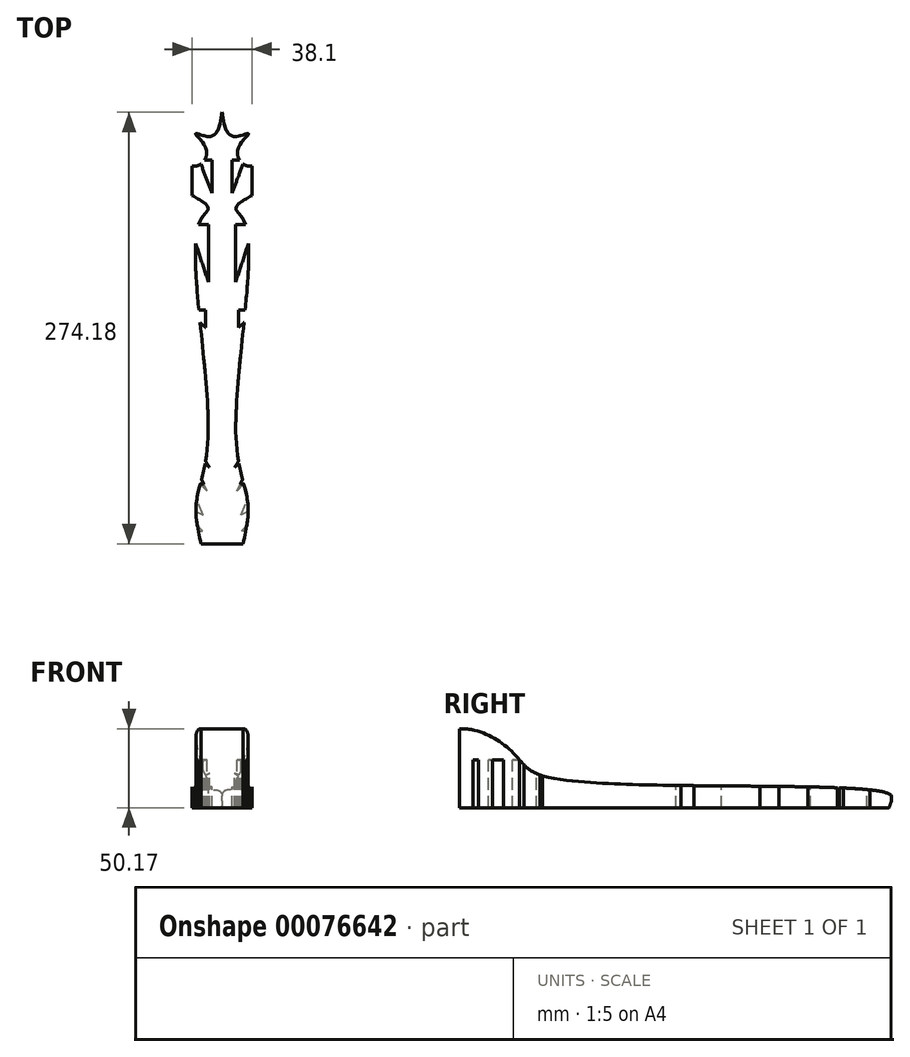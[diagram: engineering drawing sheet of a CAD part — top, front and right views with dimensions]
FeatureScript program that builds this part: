
annotation { "Feature Type Name" : "Feature", "Feature Type Description" : "" }
export const myFeature = defineFeature(function(context is Context, id is Id, definition is map)
    precondition{}
    {
        {
            var Q0;
            Q0=qCreatedBy(makeId("Right.planeOp"),FACE);
            var sketch = newSketch(context, id + "F0", { "sketchPlane" : qUnion([Q0])});
            skLineSegment(sketch, "E0", {"start": v(-121.4, 33.57) * mm, "end": v(-121.4, -30.43) * mm});
            skLineSegment(sketch, "E1", {"start": v(-121.4, -30.43) * mm, "end": v(178.6, -30.43) * mm});
            skLineSegment(sketch, "E2", {"start": v(178.6, -30.43) * mm, "end": v(178.6, -10.43) * mm});
            skLineSegment(sketch, "E3", {"start": v(178.6, -10.43) * mm, "end": v(-121.4, 33.57) * mm});
            skSolve(sketch);
        }
        {
            var Q0;
            Q0=makeQuery(id+"F0.imprint","IMPRINT",FACE,{"disambiguationData":[TD([[makeQuery(id+"F0.imprint","IMPRINT",EDGE,{"derivedFrom":sQuery(id+"F0.wireOp",EDGE,"E0")}),1.0]])]});
            extrude(context, id + "F1", {"entities" : qUnion([Q0]), "endBound" : BoundingType.SYMMETRIC, "depth" : 38.1 * mm});
        }
        {
            var Q0;
            Q0=makeQuery(id+"F1.opExtrude","CAP_FACE",FACE,{"disambiguationData":[OSD([sQuery(id+"F0.wireOp",EDGE,"E0"),sQuery(id+"F0.wireOp",EDGE,"E1"),sQuery(id+"F0.wireOp",EDGE,"E2"),sQuery(id+"F0.wireOp",EDGE,"E3")])],"isStart":false});
            var sketch = newSketch(context, id + "F2", { "sketchPlane" : qUnion([Q0])});
            skFitSpline(sketch, "E4", {"points": [v(151.33, -30.43) * mm, v(150.2, -21.07) * mm, v(-60.83, -11.96) * mm, v(-83.33, 0) * mm, v(-97.56, 12.53) * mm, v(-121.4, 19.65) * mm, v(-141.13, 15.1) * mm, v(-149.96, 23.07) * mm, v(-109.24, 93.12) * mm, v(225.94, 33.03) * mm, v(150.76, -71.76) * mm, v(151.33, -30.43) * mm]});
            skSolve(sketch);
        }
        {
            var Q0;
            {var subQ4=makeQuery(id+"F1.opExtrude","CAP_EDGE",EDGE,{"disambiguationData":[OSD([sQuery(id+"F0.wireOp",EDGE,"E2")])],"isStart":false});Q0=makeQuery(id+"F2.imprint","IMPRINT",FACE,{"disambiguationData":[TD([[makeQuery(id+"F2.imprint","IMPRINT",EDGE,{"derivedFrom":subQ4}),-1.0]])]});}
            var Q1;
            {var subQ4=makeQuery(id+"F1.opExtrude","CAP_EDGE",EDGE,{"disambiguationData":[OSD([sQuery(id+"F0.wireOp",EDGE,"E2")])],"isStart":false});Q1=makeQuery(id+"F2.imprint","IMPRINT",FACE,{"disambiguationData":[TD([[makeQuery(id+"F2.imprint","IMPRINT",EDGE,{"derivedFrom":subQ4}),1.0]])]});}
            extrude(context, id + "F3", {"entities" : qUnion([Q0, Q1]), "operationType" : NewBodyOperationType.REMOVE, "endBound" : BoundingType.THROUGH_ALL, "oppositeDirection" : true, "depth" : 25.4 * mm});
        }
        {
            var Q0;
            Q0=qCreatedBy(makeId("Top.planeOp"),FACE);
            var sketch = newSketch(context, id + "F4", { "sketchPlane" : qUnion([Q0])});
            skFitSpline(sketch, "E5", {"points": [v(12.48, -124.75) * mm, v(16.45, -96.43) * mm, v(8.78, -51.97) * mm, v(14.86, 81.41) * mm, v(8.78, 92) * mm, v(24.4, 102.59) * mm], "startDerivative": vector(42.02, 169.58) * mm, "endDerivative": vector(164.62, 83.35) * mm});
            skFitSpline(sketch, "E6", {"points": [v(24.4, 102.59) * mm, v(51.58, 102.59) * mm, v(36.6, 122.95) * mm, v(16.82, 118.49) * mm, v(10.03, 129.17) * mm, v(16.82, 139.14) * mm, v(6.87, 137.47) * mm, v(0, 152.77) * mm], "startDerivative": vector(212.7, -46.03) * mm, "endDerivative": vector(-22.94, 152.15) * mm});
            skLineSegment(sketch, "E7", {"start": v(12.48, -124.75) * mm, "end": v(0, -124.75) * mm});
            skFitSpline(sketch, "E8.MirrorCS", {"points": [v(-12.48, -124.75) * mm, v(-16.45, -96.43) * mm, v(-8.78, -51.97) * mm, v(-14.86, 81.41) * mm, v(-8.78, 92) * mm, v(-24.4, 102.59) * mm], "startDerivative": vector(-42.02, 169.58) * mm, "endDerivative": vector(-164.62, 83.35) * mm});
            skFitSpline(sketch, "E9.MirrorCS", {"points": [v(-24.4, 102.59) * mm, v(-51.58, 102.59) * mm, v(-36.6, 122.95) * mm, v(-16.82, 118.49) * mm, v(-10.03, 129.17) * mm, v(-16.82, 139.14) * mm, v(-6.87, 137.47) * mm, v(0, 152.77) * mm], "startDerivative": vector(-212.7, -46.03) * mm, "endDerivative": vector(22.94, 152.15) * mm});
            skLineSegment(sketch, "E10", {"start": v(0, -124.75) * mm, "end": v(43.37, -140.89) * mm});
            skLineSegment(sketch, "E11", {"start": v(43.37, -140.89) * mm, "end": v(74.82, 175.47) * mm});
            skLineSegment(sketch, "E12", {"start": v(74.82, 175.47) * mm, "end": v(-70.75, 175.47) * mm});
            skLineSegment(sketch, "E13", {"start": v(-70.75, 175.47) * mm, "end": v(-70.75, -122.45) * mm});
            skLineSegment(sketch, "E14", {"start": v(-70.75, -122.45) * mm, "end": v(-18.7, -143.06) * mm});
            skLineSegment(sketch, "E15", {"start": v(-18.7, -143.06) * mm, "end": v(-12.48, -124.75) * mm});
            skSolve(sketch);
        }
        {
            var Q0;
            Q0=makeQuery(id+"F4.imprint","IMPRINT",FACE,{"disambiguationData":[TD([[makeQuery(id+"F4.imprint","IMPRINT",EDGE,{"derivedFrom":sQuery(id+"F4.wireOp",EDGE,"E5")}),-1.0]])]});
            extrude(context, id + "F5", {"entities" : qUnion([Q0]), "operationType" : NewBodyOperationType.REMOVE, "endBound" : BoundingType.SYMMETRIC, "oppositeDirection" : true, "depth" : 3657.6 * mm});
        }
        {
            var Q0;
            Q0=qCreatedBy(makeId("Top.planeOp"),FACE);
            var sketch = newSketch(context, id + "F6", { "sketchPlane" : qUnion([Q0])});
            skLineSegment(sketch, "E16", {"start": v(14.44, 122.24) * mm, "end": v(6.22, 122.24) * mm});
            skLineSegment(sketch, "E17", {"start": v(6.22, 122.24) * mm, "end": v(6.22, 101.46) * mm});
            skLineSegment(sketch, "E18", {"start": v(6.22, 101.46) * mm, "end": v(14.44, 122.24) * mm});
            skLineSegment(sketch, "E19", {"start": v(20.7, 81.28) * mm, "end": v(8.6, 81.28) * mm});
            skLineSegment(sketch, "E20", {"start": v(8.6, 81.28) * mm, "end": v(8.6, 44.72) * mm});
            skLineSegment(sketch, "E21", {"start": v(8.6, 44.72) * mm, "end": v(20.7, 81.28) * mm});
            skLineSegment(sketch, "E22", {"start": v(22.58, 27.24) * mm, "end": v(10.49, 27.24) * mm});
            skLineSegment(sketch, "E23", {"start": v(10.49, 27.24) * mm, "end": v(10.49, 15.95) * mm});
            skLineSegment(sketch, "E24", {"start": v(22.58, 27.24) * mm, "end": v(10.49, 15.95) * mm});
            skLineSegment(sketch, "E25", {"start": v(12.37, -127.9) * mm, "end": v(20.97, -113.1) * mm});
            skLineSegment(sketch, "E26", {"start": v(20.97, -113.1) * mm, "end": v(12.37, -113.1) * mm});
            skLineSegment(sketch, "E27", {"start": v(12.37, -113.1) * mm, "end": v(30.65, -93.2) * mm});
            skLineSegment(sketch, "E28", {"start": v(30.65, -93.2) * mm, "end": v(12.1, -103.16) * mm});
            skPoint(sketch, "E28.endSnap0", {"position": v(21.5, -103.16) * mm});
            skLineSegment(sketch, "E29", {"start": v(12.1, -103.16) * mm, "end": v(24.73, -72.5) * mm});
            skLineSegment(sketch, "E30", {"start": v(24.73, -72.5) * mm, "end": v(9.41, -87.83) * mm});
            skPoint(sketch, "E30.endSnap0", {"position": v(18.42, -87.83) * mm});
            skLineSegment(sketch, "E31", {"start": v(9.41, -87.83) * mm, "end": v(24.2, -57.72) * mm});
            skLineSegment(sketch, "E32", {"start": v(24.2, -57.72) * mm, "end": v(8.07, -72.77) * mm});
            skPoint(sketch, "E32.endSnap0", {"position": v(16.8, -72.77) * mm});
            skLineSegment(sketch, "E33", {"start": v(8.07, -72.77) * mm, "end": v(32, -33.79) * mm});
            skLineSegment(sketch, "E34", {"start": v(32, -33.79) * mm, "end": v(60.44, -51.25) * mm});
            skLineSegment(sketch, "E35", {"start": v(60.44, -51.25) * mm, "end": v(41.67, -110.68) * mm});
            skLineSegment(sketch, "E36", {"start": v(41.67, -110.68) * mm, "end": v(12.37, -127.9) * mm});
            skLineSegment(sketch, "E37.MirrorCS", {"start": v(-6.22, 122.24) * mm, "end": v(-6.22, 101.46) * mm});
            skLineSegment(sketch, "E38.MirrorCS", {"start": v(-14.44, 122.24) * mm, "end": v(-6.22, 122.24) * mm});
            skLineSegment(sketch, "E39.MirrorCS", {"start": v(-6.22, 101.46) * mm, "end": v(-14.44, 122.24) * mm});
            skLineSegment(sketch, "E40.MirrorCS", {"start": v(-8.6, 81.28) * mm, "end": v(-8.6, 44.72) * mm});
            skLineSegment(sketch, "E41.MirrorCS", {"start": v(-20.7, 81.28) * mm, "end": v(-8.6, 81.28) * mm});
            skLineSegment(sketch, "E42.MirrorCS", {"start": v(-8.6, 44.72) * mm, "end": v(-20.7, 81.28) * mm});
            skLineSegment(sketch, "E43.MirrorCS", {"start": v(-10.49, 27.24) * mm, "end": v(-10.49, 15.95) * mm});
            skLineSegment(sketch, "E44.MirrorCS", {"start": v(-22.58, 27.24) * mm, "end": v(-10.49, 27.24) * mm});
            skLineSegment(sketch, "E45.MirrorCS", {"start": v(-22.58, 27.24) * mm, "end": v(-10.49, 15.95) * mm});
            skLineSegment(sketch, "E46.MirrorCS", {"start": v(-8.07, -72.77) * mm, "end": v(-32, -33.79) * mm});
            skLineSegment(sketch, "E47.MirrorCS", {"start": v(-32, -33.79) * mm, "end": v(-60.44, -51.25) * mm});
            skLineSegment(sketch, "E48.MirrorCS", {"start": v(-60.44, -51.25) * mm, "end": v(-41.67, -110.68) * mm});
            skLineSegment(sketch, "E49.MirrorCS", {"start": v(-41.67, -110.68) * mm, "end": v(-12.37, -127.9) * mm});
            skLineSegment(sketch, "E50.MirrorCS", {"start": v(-12.37, -127.9) * mm, "end": v(-20.97, -113.1) * mm});
            skLineSegment(sketch, "E51.MirrorCS", {"start": v(-20.97, -113.1) * mm, "end": v(-12.37, -113.1) * mm});
            skLineSegment(sketch, "E52.MirrorCS", {"start": v(-12.37, -113.1) * mm, "end": v(-30.65, -93.2) * mm});
            skLineSegment(sketch, "E53.MirrorCS", {"start": v(-30.65, -93.2) * mm, "end": v(-12.1, -103.16) * mm});
            skLineSegment(sketch, "E54.MirrorCS", {"start": v(-12.1, -103.16) * mm, "end": v(-24.73, -72.5) * mm});
            skLineSegment(sketch, "E55.MirrorCS", {"start": v(-24.73, -72.5) * mm, "end": v(-9.41, -87.83) * mm});
            skLineSegment(sketch, "E56.MirrorCS", {"start": v(-9.41, -87.83) * mm, "end": v(-24.2, -57.72) * mm});
            skLineSegment(sketch, "E57.MirrorCS", {"start": v(-24.2, -57.72) * mm, "end": v(-8.07, -72.77) * mm});
            skSolve(sketch);
        }
        {
            var Q0;
            Q0=makeQuery(id+"F6.imprint","IMPRINT",FACE,{"disambiguationData":[TD([[makeQuery(id+"F6.imprint","IMPRINT",EDGE,{"derivedFrom":sQuery(id+"F6.wireOp",EDGE,"E25")}),-1.0]])]});
            var Q1;
            Q1=makeQuery(id+"F6.imprint","IMPRINT",FACE,{"disambiguationData":[TD([[makeQuery(id+"F6.imprint","IMPRINT",EDGE,{"derivedFrom":sQuery(id+"F6.wireOp",EDGE,"E19")}),1.0]])]});
            var Q2;
            Q2=makeQuery(id+"F6.imprint","IMPRINT",FACE,{"disambiguationData":[TD([[makeQuery(id+"F6.imprint","IMPRINT",EDGE,{"derivedFrom":sQuery(id+"F6.wireOp",EDGE,"E37.MirrorCS")}),-1.0]])]});
            var Q3;
            Q3=makeQuery(id+"F6.imprint","IMPRINT",FACE,{"disambiguationData":[TD([[makeQuery(id+"F6.imprint","IMPRINT",EDGE,{"derivedFrom":sQuery(id+"F6.wireOp",EDGE,"E22")}),1.0]])]});
            var Q4;
            Q4=makeQuery(id+"F6.imprint","IMPRINT",FACE,{"disambiguationData":[TD([[makeQuery(id+"F6.imprint","IMPRINT",EDGE,{"derivedFrom":sQuery(id+"F6.wireOp",EDGE,"E46.MirrorCS")}),1.0]])]});
            var Q5;
            Q5=makeQuery(id+"F6.imprint","IMPRINT",FACE,{"disambiguationData":[TD([[makeQuery(id+"F6.imprint","IMPRINT",EDGE,{"derivedFrom":sQuery(id+"F6.wireOp",EDGE,"E43.MirrorCS")}),-1.0]])]});
            var Q6;
            Q6=makeQuery(id+"F6.imprint","IMPRINT",FACE,{"disambiguationData":[TD([[makeQuery(id+"F6.imprint","IMPRINT",EDGE,{"derivedFrom":sQuery(id+"F6.wireOp",EDGE,"E16")}),1.0]])]});
            var Q7;
            Q7=makeQuery(id+"F6.imprint","IMPRINT",FACE,{"disambiguationData":[TD([[makeQuery(id+"F6.imprint","IMPRINT",EDGE,{"derivedFrom":sQuery(id+"F6.wireOp",EDGE,"E40.MirrorCS")}),-1.0]])]});
            extrude(context, id + "F7", {"entities" : qUnion([Q0, Q1, Q2, Q3, Q4, Q5, Q6, Q7]), "operationType" : NewBodyOperationType.REMOVE, "endBound" : BoundingType.THROUGH_ALL, "oppositeDirection" : true, "depth" : 25.4 * mm});
        }
    });
